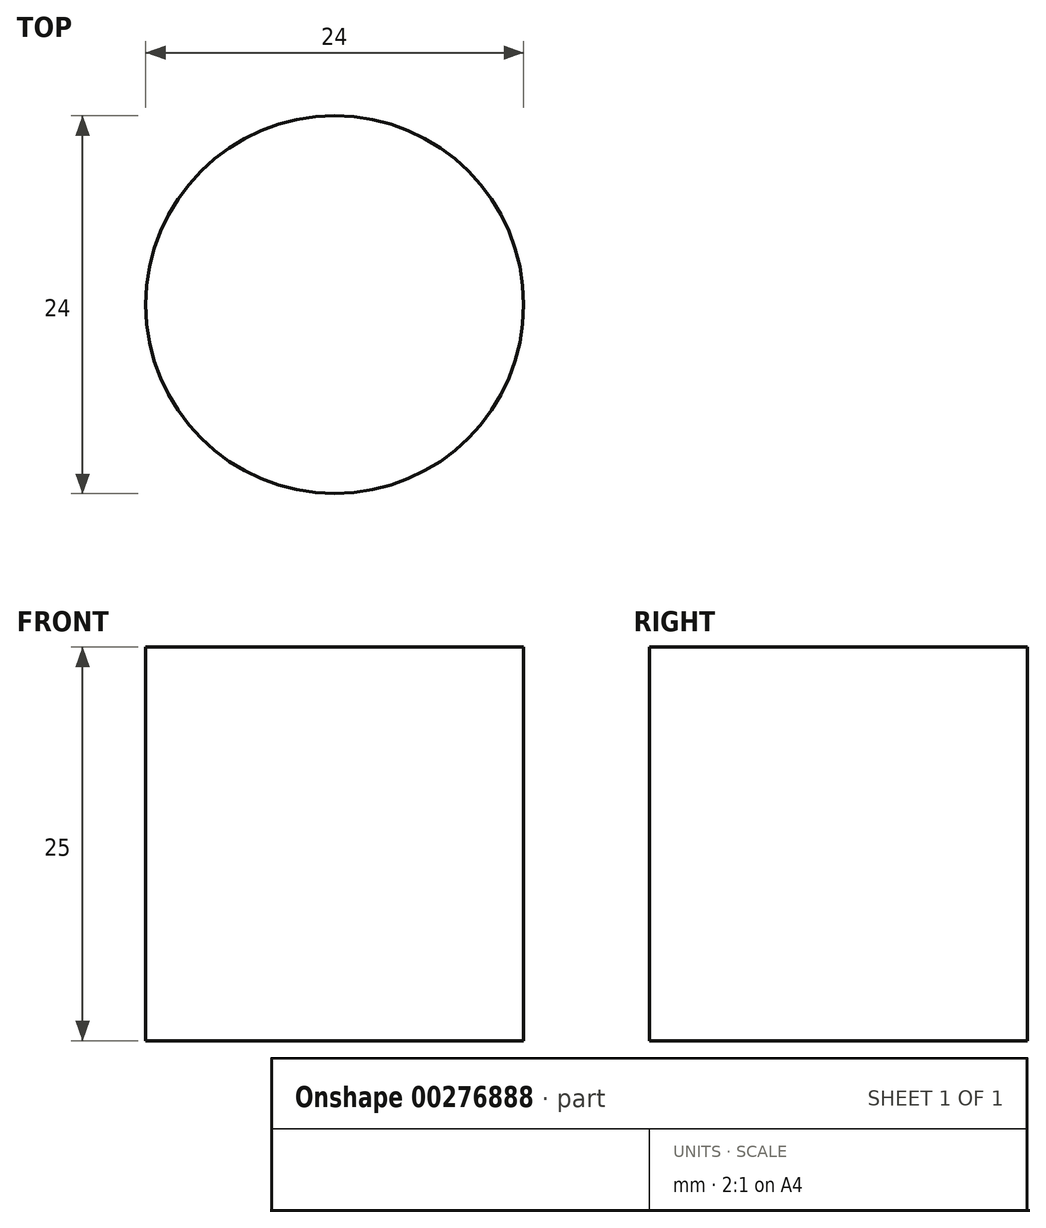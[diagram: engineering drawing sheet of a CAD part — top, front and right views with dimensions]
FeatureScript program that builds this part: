
annotation { "Feature Type Name" : "Feature", "Feature Type Description" : "" }
export const myFeature = defineFeature(function(context is Context, id is Id, definition is map)
    precondition{}
    {
        {
            var Q0;
            Q0=qCreatedBy(makeId("Top.planeOp"),FACE);
            var sketch = newSketch(context, id + "F0", { "sketchPlane" : qUnion([Q0])});
            skLineSegment(sketch, "E0", {"start": v(-57.13, -20) * mm, "end": v(102.87, -20) * mm});
            skLineSegment(sketch, "E1", {"start": v(102.87, -20) * mm, "end": v(102.87, 80) * mm});
            skLineSegment(sketch, "E2", {"start": v(102.87, 80) * mm, "end": v(52.87, 80) * mm});
            skLineSegment(sketch, "E3", {"start": v(52.87, 80) * mm, "end": v(52.87, 50) * mm});
            skLineSegment(sketch, "E4", {"start": v(32.87, 30) * mm, "end": v(12.87, 30) * mm});
            skLineSegment(sketch, "E5", {"start": v(-7.13, 50) * mm, "end": v(-7.13, 80) * mm});
            skLineSegment(sketch, "E6", {"start": v(-7.13, 80) * mm, "end": v(-57.13, 80) * mm});
            skLineSegment(sketch, "E7", {"start": v(-57.13, 80) * mm, "end": v(-57.13, -20) * mm});
            skPoint(sketch, "E8.visualSharp", {"position": v(-7.13, 30) * mm});
            skArc(sketch, "E8.filletArc", {"start": v(-7.13, 50) * mm, "mid": v(-1.27, 35.86) * mm, "end": v(12.87, 30) * mm});
            skPoint(sketch, "E9.visualSharp", {"position": v(52.87, 30) * mm});
            skArc(sketch, "E9.filletArc", {"start": v(32.87, 30) * mm, "mid": v(47.01, 35.86) * mm, "end": v(52.87, 50) * mm});
            skPoint(sketch, "E10", {"position": v(77.87, 7.17) * mm});
            skCircle(sketch, "E11", {"center": v(77.87, 7.17) * mm, "radius": 12 * mm});
            skCircle(sketch, "E12.cCircle", {"center": v(77.87, 7.17) * mm, "radius": 12 * mm, "construction": true});
            skLineSegment(sketch, "E12.0", {"start": v(91.72, 6.86) * mm, "end": v(84.53, -4.98) * mm});
            skLineSegment(sketch, "E12.1", {"start": v(84.53, -4.98) * mm, "end": v(70.68, -4.67) * mm});
            skLineSegment(sketch, "E12.2", {"start": v(70.68, -4.67) * mm, "end": v(64.02, 7.48) * mm});
            skLineSegment(sketch, "E12.3", {"start": v(64.02, 7.48) * mm, "end": v(71.21, 19.32) * mm});
            skLineSegment(sketch, "E12.4", {"start": v(71.21, 19.32) * mm, "end": v(85.06, 19.01) * mm});
            skLineSegment(sketch, "E12.5", {"start": v(85.06, 19.01) * mm, "end": v(91.72, 6.86) * mm});
            skPoint(sketch, "E12.0.midPoint", {"position": v(88.13, 0.94) * mm});
            skLineSegment(sketch, "E13", {"start": v(102.87, -20) * mm, "end": v(102.87, 55) * mm});
            skCircle(sketch, "E14", {"center": v(77.87, 62.17) * mm, "radius": 12 * mm});
            skCircle(sketch, "E15.cCircle", {"center": v(77.87, 62.17) * mm, "radius": 12 * mm, "construction": true});
            skLineSegment(sketch, "E15.0", {"start": v(70.94, 74.17) * mm, "end": v(84.8, 74.17) * mm});
            skLineSegment(sketch, "E15.1", {"start": v(84.8, 74.17) * mm, "end": v(91.73, 62.17) * mm});
            skLineSegment(sketch, "E15.2", {"start": v(91.73, 62.17) * mm, "end": v(84.8, 50.17) * mm});
            skLineSegment(sketch, "E15.3", {"start": v(84.8, 50.17) * mm, "end": v(70.94, 50.17) * mm});
            skLineSegment(sketch, "E15.4", {"start": v(70.94, 50.17) * mm, "end": v(64.01, 62.17) * mm});
            skLineSegment(sketch, "E15.5", {"start": v(64.01, 62.17) * mm, "end": v(70.94, 74.17) * mm});
            skPoint(sketch, "E15.0.midPoint", {"position": v(77.87, 74.17) * mm});
            skLineSegment(sketch, "E16", {"start": v(-57.13, -20) * mm, "end": v(-57.13, 0) * mm});
            skLineSegment(sketch, "E17", {"start": v(-57.13, 0) * mm, "end": v(-57.13, 55) * mm});
            skLineSegment(sketch, "E18", {"start": v(-45.99, 55) * mm, "end": v(-44.13, 55) * mm});
            skCircle(sketch, "E19", {"center": v(-32.13, 55) * mm, "radius": 12 * mm});
            skCircle(sketch, "E20.cCircle", {"center": v(-32.13, 55) * mm, "radius": 12 * mm, "construction": true});
            skLineSegment(sketch, "E20.0", {"start": v(-39.06, 67) * mm, "end": v(-25.2, 67) * mm});
            skLineSegment(sketch, "E20.1", {"start": v(-25.2, 67) * mm, "end": v(-18.27, 55) * mm});
            skLineSegment(sketch, "E20.2", {"start": v(-18.27, 55) * mm, "end": v(-25.2, 43) * mm});
            skLineSegment(sketch, "E20.3", {"start": v(-25.2, 43) * mm, "end": v(-39.06, 43) * mm});
            skLineSegment(sketch, "E20.4", {"start": v(-39.06, 43) * mm, "end": v(-45.99, 55) * mm});
            skLineSegment(sketch, "E20.5", {"start": v(-45.99, 55) * mm, "end": v(-39.06, 67) * mm});
            skPoint(sketch, "E20.0.midPoint", {"position": v(-32.13, 67) * mm});
            skCircle(sketch, "E21", {"center": v(-32.13, 7.17) * mm, "radius": 12 * mm});
            skCircle(sketch, "E22.cCircle", {"center": v(-32.13, 7.17) * mm, "radius": 12 * mm, "construction": true});
            skLineSegment(sketch, "E22.0", {"start": v(-39.06, 19.17) * mm, "end": v(-25.2, 19.17) * mm});
            skLineSegment(sketch, "E22.1", {"start": v(-25.2, 19.17) * mm, "end": v(-18.27, 7.17) * mm});
            skLineSegment(sketch, "E22.2", {"start": v(-18.27, 7.17) * mm, "end": v(-25.2, -4.83) * mm});
            skLineSegment(sketch, "E22.3", {"start": v(-25.2, -4.83) * mm, "end": v(-39.06, -4.83) * mm});
            skLineSegment(sketch, "E22.4", {"start": v(-39.06, -4.83) * mm, "end": v(-45.99, 7.17) * mm});
            skLineSegment(sketch, "E22.5", {"start": v(-45.99, 7.17) * mm, "end": v(-39.06, 19.17) * mm});
            skPoint(sketch, "E22.0.midPoint", {"position": v(-32.13, 19.17) * mm});
            skLineSegment(sketch, "E23", {"start": v(-57.13, -20) * mm, "end": v(-2.13, -20) * mm});
            skPoint(sketch, "E24.end.orphan", {"position": v(-2.13, 0) * mm});
            skArc(sketch, "E25", {"start": v(47.87, -2.5) * mm, "mid": v(50.37, 0) * mm, "end": v(47.87, 2.5) * mm});
            skArc(sketch, "E26", {"start": v(-2.13, 2.5) * mm, "mid": v(-4.63, 0) * mm, "end": v(-2.13, -2.5) * mm});
            skLineSegment(sketch, "E27", {"start": v(47.87, 2.5) * mm, "end": v(-2.13, 2.5) * mm});
            skLineSegment(sketch, "E28", {"start": v(-2.13, -2.5) * mm, "end": v(47.87, -2.5) * mm});
            skSolve(sketch);
        }
        {
            var Q0;
            {var subQ0=sQuery(id+"F0.wireOp",EDGE,"E19");var subQ4=makeQuery(id+"F0.imprint","INTERSECT",VERTEX,{"derivedFrom":[subQ0,sQuery(id+"F0.wireOp",EDGE,"E20.0")]});Q0=makeQuery(id+"F0.imprint","IMPRINT",FACE,{"disambiguationData":[TD([[makeQuery(id+"F0.imprint","IMPRINT",EDGE,{"disambiguationData":[TD([[subQ4,1.0]])],"derivedFrom":subQ0}),1.0]])]});}
            extrude(context, id + "F1", {"entities" : qUnion([Q0]), "depth" : 25 * mm});
        }
    });
